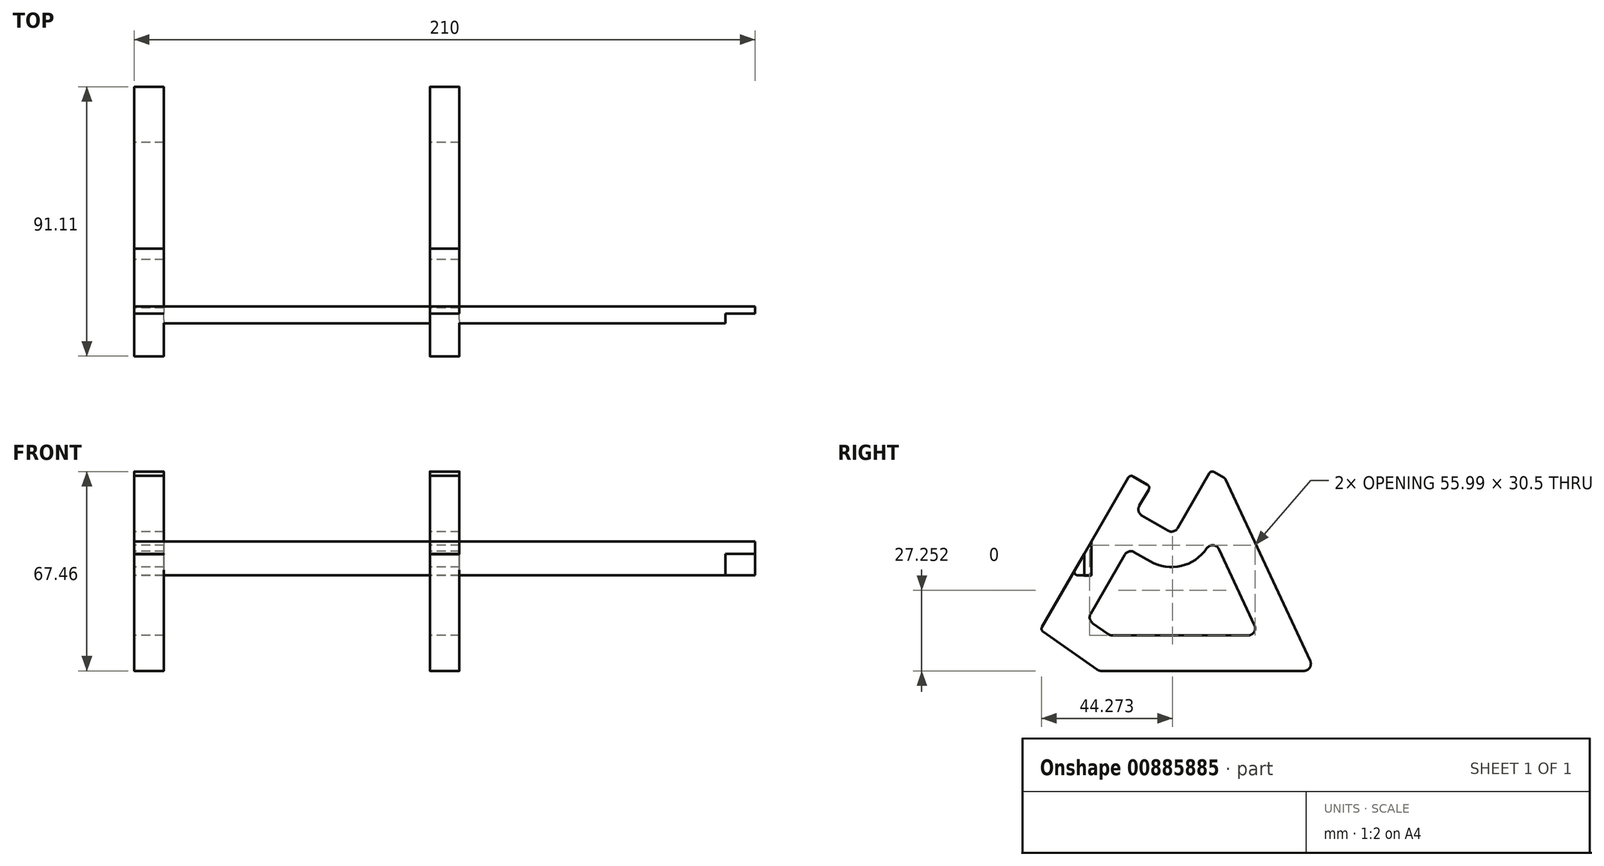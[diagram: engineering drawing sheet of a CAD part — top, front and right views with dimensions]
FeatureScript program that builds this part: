
annotation { "Feature Type Name" : "Feature", "Feature Type Description" : "" }
export const myFeature = defineFeature(function(context is Context, id is Id, definition is map)
    precondition{}
    {
        {
            var Q0;
            Q0=qCreatedBy(makeId("Right.planeOp"),FACE);
            var sketch = newSketch(context, id + "F0", { "sketchPlane" : qUnion([Q0])});
            skLineSegment(sketch, "E0", {"start": v(-36.35, 13.26) * mm, "end": v(-18.04, 0.43) * mm});
            skLineSegment(sketch, "E1", {"start": v(-16.66, 0) * mm, "end": v(-10.97, 0) * mm});
            skLineSegment(sketch, "E2", {"start": v(24.9, 65.35) * mm, "end": v(21.53, 67.3) * mm});
            skLineSegment(sketch, "E3", {"start": v(19.9, 66.86) * mm, "end": v(9.2, 48.33) * mm});
            skLineSegment(sketch, "E4", {"start": v(-3.8, 55.83) * mm, "end": v(-0.6, 61.37) * mm});
            skLineSegment(sketch, "E5", {"start": v(-1.04, 63.01) * mm, "end": v(-5.86, 65.8) * mm});
            skLineSegment(sketch, "E6", {"start": v(-7.54, 65.34) * mm, "end": v(-19.98, 43.8) * mm});
            skLineSegment(sketch, "E7", {"start": v(-2.92, 52.55) * mm, "end": v(5.91, 47.45) * mm});
            skLineSegment(sketch, "E8", {"start": v(10.16, 50) * mm, "end": v(1.5, 50) * mm, "construction": true});
            skPoint(sketch, "E9.visualSharp", {"position": v(8, 46.25) * mm});
            skArc(sketch, "E9.filletArc", {"start": v(5.91, 47.45) * mm, "mid": v(7.73, 47.21) * mm, "end": v(9.2, 48.33) * mm});
            skPoint(sketch, "E10.visualSharp", {"position": v(-5, 53.75) * mm});
            skArc(sketch, "E10.filletArc", {"start": v(-3.8, 55.83) * mm, "mid": v(-4.04, 54) * mm, "end": v(-2.92, 52.55) * mm});
            skPoint(sketch, "E11.visualSharp", {"position": v(25.23, 65.16) * mm});
            skPoint(sketch, "E12.visualSharp", {"position": v(20.5, 67.9) * mm});
            skArc(sketch, "E12.filletArc", {"start": v(21.53, 67.3) * mm, "mid": v(20.62, 67.42) * mm, "end": v(19.9, 66.86) * mm});
            skPoint(sketch, "E13.visualSharp", {"position": v(0, 62.41) * mm});
            skArc(sketch, "E13.filletArc", {"start": v(-0.6, 61.37) * mm, "mid": v(-0.48, 62.28) * mm, "end": v(-1.04, 63.01) * mm});
            skPoint(sketch, "E14.visualSharp", {"position": v(-6.93, 66.41) * mm});
            skArc(sketch, "E14.filletArc", {"start": v(-5.86, 65.8) * mm, "mid": v(-6.8, 65.92) * mm, "end": v(-7.54, 65.34) * mm});
            skPoint(sketch, "E15.visualSharp", {"position": v(-37.25, 13.89) * mm});
            skArc(sketch, "E15.filletArc", {"start": v(-36.7, 14.84) * mm, "mid": v(-36.83, 13.98) * mm, "end": v(-36.35, 13.26) * mm});
            skLineSegment(sketch, "E16", {"start": v(-10.97, 0) * mm, "end": v(21.5, 0) * mm});
            skLineSegment(sketch, "E17", {"start": v(25.4, 64.82) * mm, "end": v(54.02, 3.41) * mm});
            skLineSegment(sketch, "E18", {"start": v(51.85, 0) * mm, "end": v(21.5, 0) * mm});
            skArc(sketch, "E19.filletArc", {"start": v(25.4, 64.82) * mm, "mid": v(25.19, 65.12) * mm, "end": v(24.9, 65.35) * mm});
            skLineSegment(sketch, "E20.0", {"start": v(14.51, 59.75) * mm, "end": v(15.08, 58.53) * mm});
            skLineSegment(sketch, "E21.0", {"start": v(-12.88, 12) * mm, "end": v(33.01, 12) * mm});
            skLineSegment(sketch, "E22.0", {"start": v(-19.56, 16.15) * mm, "end": v(-14.25, 12.43) * mm});
            skLineSegment(sketch, "E23.1", {"start": v(-5.46, 40.16) * mm, "end": v(-0.09, 37.06) * mm});
            skArc(sketch, "E23.2", {"start": v(-0.09, 37.06) * mm, "mid": v(10.34, 35.5) * mm, "end": v(19.04, 41.46) * mm});
            skLineSegment(sketch, "E23.3", {"start": v(28.6, 57.94) * mm, "end": v(27.78, 56.53) * mm});
            skLineSegment(sketch, "E24.trimOffspring", {"start": v(23.2, 41.13) * mm, "end": v(35.19, 15.41) * mm});
            skLineSegment(sketch, "E25.trimOffspring", {"start": v(-8.74, 39.28) * mm, "end": v(-20.26, 19.32) * mm});
            skPoint(sketch, "E26.visualSharp", {"position": v(21.02, 45.8) * mm});
            skArc(sketch, "E26.filletArc", {"start": v(23.2, 41.13) * mm, "mid": v(21.21, 42.5) * mm, "end": v(19.04, 41.46) * mm});
            skPoint(sketch, "E27.visualSharp", {"position": v(36.78, 12) * mm});
            skArc(sketch, "E27.filletArc", {"start": v(33.01, 12) * mm, "mid": v(35.04, 13.11) * mm, "end": v(35.19, 15.41) * mm});
            skPoint(sketch, "E28.visualSharp", {"position": v(-13.63, 12) * mm});
            skArc(sketch, "E28.filletArc", {"start": v(-14.25, 12.43) * mm, "mid": v(-13.6, 12.11) * mm, "end": v(-12.88, 12) * mm});
            skPoint(sketch, "E29.visualSharp", {"position": v(-21.36, 17.41) * mm});
            skArc(sketch, "E29.filletArc", {"start": v(-20.26, 19.32) * mm, "mid": v(-20.53, 17.6) * mm, "end": v(-19.56, 16.15) * mm});
            skPoint(sketch, "E30.visualSharp", {"position": v(-7.54, 41.36) * mm});
            skArc(sketch, "E30.filletArc", {"start": v(-5.46, 40.16) * mm, "mid": v(-7.28, 40.4) * mm, "end": v(-8.74, 39.28) * mm});
            skPoint(sketch, "E31.visualSharp", {"position": v(55.62, 0) * mm});
            skArc(sketch, "E31.filletArc", {"start": v(51.85, 0) * mm, "mid": v(53.87, 1.11) * mm, "end": v(54.02, 3.41) * mm});
            skPoint(sketch, "E32.visualSharp", {"position": v(-17.42, 0) * mm});
            skArc(sketch, "E32.filletArc", {"start": v(-18.04, 0.43) * mm, "mid": v(-17.38, 0.11) * mm, "end": v(-16.66, 0) * mm});
            skLineSegment(sketch, "E33", {"start": v(-19.98, 43.8) * mm, "end": v(-19.98, 32.26) * mm});
            skLineSegment(sketch, "E34", {"start": v(-19.98, 32.26) * mm, "end": v(-22.48, 32.26) * mm});
            skLineSegment(sketch, "E35", {"start": v(-22.48, 32.26) * mm, "end": v(-22.48, 39.48) * mm});
            skLineSegment(sketch, "E36.trimOffspring", {"start": v(-22.48, 39.48) * mm, "end": v(-36.7, 14.84) * mm});
            skSolve(sketch);
        }
        {
            var Q0;
            Q0=makeQuery(id+"F0.imprint","IMPRINT",FACE,{"disambiguationData":[TD([[makeQuery(id+"F0.imprint","IMPRINT",EDGE,{"derivedFrom":sQuery(id+"F0.wireOp",EDGE,"E0")}),1.0]])]});
            extrude(context, id + "F1", {"entities" : qUnion([Q0]), "depth" : 10 * mm, "offsetDistance" : 25 * mm});
        }
        {
            var Q0;
            Q0=makeQuery(id+"F1.opExtrude","CAP_FACE",FACE,{"disambiguationData":[OSD([sQuery(id+"F0.wireOp",EDGE,"E0"),sQuery(id+"F0.wireOp",EDGE,"E1"),sQuery(id+"F0.wireOp",EDGE,"E2"),sQuery(id+"F0.wireOp",EDGE,"E3"),sQuery(id+"F0.wireOp",EDGE,"E4"),sQuery(id+"F0.wireOp",EDGE,"E5"),sQuery(id+"F0.wireOp",EDGE,"E6"),sQuery(id+"F0.wireOp",EDGE,"E7"),sQuery(id+"F0.wireOp",EDGE,"E9.filletArc"),sQuery(id+"F0.wireOp",EDGE,"E10.filletArc"),sQuery(id+"F0.wireOp",EDGE,"E12.filletArc"),sQuery(id+"F0.wireOp",EDGE,"E13.filletArc"),sQuery(id+"F0.wireOp",EDGE,"E14.filletArc"),sQuery(id+"F0.wireOp",EDGE,"E15.filletArc"),sQuery(id+"F0.wireOp",EDGE,"E16"),sQuery(id+"F0.wireOp",EDGE,"E17"),sQuery(id+"F0.wireOp",EDGE,"E18"),sQuery(id+"F0.wireOp",EDGE,"E19.filletArc"),sQuery(id+"F0.wireOp",EDGE,"E21.0"),sQuery(id+"F0.wireOp",EDGE,"E22.0"),sQuery(id+"F0.wireOp",EDGE,"E23.1"),sQuery(id+"F0.wireOp",EDGE,"E23.2"),sQuery(id+"F0.wireOp",EDGE,"E24.trimOffspring"),sQuery(id+"F0.wireOp",EDGE,"E25.trimOffspring"),sQuery(id+"F0.wireOp",EDGE,"E26.filletArc"),sQuery(id+"F0.wireOp",EDGE,"E27.filletArc"),sQuery(id+"F0.wireOp",EDGE,"E28.filletArc"),sQuery(id+"F0.wireOp",EDGE,"E29.filletArc"),sQuery(id+"F0.wireOp",EDGE,"E30.filletArc"),sQuery(id+"F0.wireOp",EDGE,"E31.filletArc"),sQuery(id+"F0.wireOp",EDGE,"E32.filletArc"),sQuery(id+"F0.wireOp",EDGE,"E33"),sQuery(id+"F0.wireOp",EDGE,"E34"),sQuery(id+"F0.wireOp",EDGE,"E35"),sQuery(id+"F0.wireOp",EDGE,"E36.trimOffspring")])],"isStart":true});
            var sketch = newSketch(context, id + "F2", { "sketchPlane" : qUnion([Q0])});
            skLineSegment(sketch, "E37.0", {"start": v(22.43, 32.3) * mm, "end": v(22.43, 39.56) * mm});
            skLineSegment(sketch, "E37.1", {"start": v(20.03, 32.3) * mm, "end": v(22.43, 32.3) * mm});
            skLineSegment(sketch, "E37.2", {"start": v(20.03, 43.72) * mm, "end": v(20.03, 32.3) * mm});
            skLineSegment(sketch, "E38", {"start": v(20.03, 43.72) * mm, "end": v(22.43, 39.56) * mm});
            skSolve(sketch);
        }
        {
            var Q0;
            Q0 = qSketchRegion(id + "F2", true);
            extrude(context, id + "F3", {"entities" : qUnion([Q0]), "operationType" : NewBodyOperationType.ADD, "oppositeDirection" : true, "depth" : 110 * mm, "offsetDistance" : 25 * mm});
        }
        {
            var Q0;
            Q0=makeQuery(id+"F3.opExtrude","CAP_FACE",FACE,{"disambiguationData":[OSD([sQuery(id+"F2.wireOp",EDGE,"E37.0"),sQuery(id+"F2.wireOp",EDGE,"E37.1"),sQuery(id+"F2.wireOp",EDGE,"E37.2"),sQuery(id+"F2.wireOp",EDGE,"E38")])],"isStart":true});
            cPlane(context, id + "F4", {"entities" : qUnion([Q0]), "cplaneType" : CPlaneType.OFFSET, "offset" : 10 * mm, "oppositeDirection" : true, "width" : 150 * mm, "height" : 150 * mm});
        }
        {
            var Q0;
            Q0=qCreatedBy(id+"F4.planeOp",FACE);
            var sketch = newSketch(context, id + "F5", { "sketchPlane" : qUnion([Q0])});
            skLineSegment(sketch, "E39.0", {"start": v(22.43, 32.3) * mm, "end": v(22.43, 39.56) * mm});
            skLineSegment(sketch, "E40", {"start": v(22.43, 39.56) * mm, "end": v(25.58, 34.1) * mm});
            skLineSegment(sketch, "E41", {"start": v(24.54, 32.3) * mm, "end": v(22.43, 32.3) * mm});
            skPoint(sketch, "E42.visualSharp", {"position": v(26.62, 32.3) * mm});
            skArc(sketch, "E42.filletArc", {"start": v(24.54, 32.3) * mm, "mid": v(25.58, 32.9) * mm, "end": v(25.58, 34.1) * mm});
            skSolve(sketch);
        }
        {
            var Q0;
            Q0=makeQuery(id+"F5.imprint","IMPRINT",FACE,{"disambiguationData":[TD([[makeQuery(id+"F5.imprint","IMPRINT",EDGE,{"derivedFrom":sQuery(id+"F5.wireOp",EDGE,"E39.0")}),-1.0]])]});
            extrude(context, id + "F6", {"entities" : qUnion([Q0]), "operationType" : NewBodyOperationType.ADD, "oppositeDirection" : true, "depth" : 90 * mm, "offsetDistance" : 25 * mm});
        }
        {
            var Q0;
            Q0=makeQuery(id+"F1.opExtrude","SWEPT_BODY",BODY,{"disambiguationData":[OSD([sQuery(id+"F0.wireOp",EDGE,"E0"),sQuery(id+"F0.wireOp",EDGE,"E1"),sQuery(id+"F0.wireOp",EDGE,"E2"),sQuery(id+"F0.wireOp",EDGE,"E3"),sQuery(id+"F0.wireOp",EDGE,"E4"),sQuery(id+"F0.wireOp",EDGE,"E5"),sQuery(id+"F0.wireOp",EDGE,"E6"),sQuery(id+"F0.wireOp",EDGE,"E7"),sQuery(id+"F0.wireOp",EDGE,"E9.filletArc"),sQuery(id+"F0.wireOp",EDGE,"E10.filletArc"),sQuery(id+"F0.wireOp",EDGE,"E12.filletArc"),sQuery(id+"F0.wireOp",EDGE,"E13.filletArc"),sQuery(id+"F0.wireOp",EDGE,"E14.filletArc"),sQuery(id+"F0.wireOp",EDGE,"E15.filletArc"),sQuery(id+"F0.wireOp",EDGE,"E16"),sQuery(id+"F0.wireOp",EDGE,"E17"),sQuery(id+"F0.wireOp",EDGE,"E18"),sQuery(id+"F0.wireOp",EDGE,"E19.filletArc"),sQuery(id+"F0.wireOp",EDGE,"E21.0"),sQuery(id+"F0.wireOp",EDGE,"E22.0"),sQuery(id+"F0.wireOp",EDGE,"E23.1"),sQuery(id+"F0.wireOp",EDGE,"E23.2"),sQuery(id+"F0.wireOp",EDGE,"E24.trimOffspring"),sQuery(id+"F0.wireOp",EDGE,"E25.trimOffspring"),sQuery(id+"F0.wireOp",EDGE,"E26.filletArc"),sQuery(id+"F0.wireOp",EDGE,"E27.filletArc"),sQuery(id+"F0.wireOp",EDGE,"E28.filletArc"),sQuery(id+"F0.wireOp",EDGE,"E29.filletArc"),sQuery(id+"F0.wireOp",EDGE,"E30.filletArc"),sQuery(id+"F0.wireOp",EDGE,"E31.filletArc"),sQuery(id+"F0.wireOp",EDGE,"E32.filletArc"),sQuery(id+"F0.wireOp",EDGE,"E33"),sQuery(id+"F0.wireOp",EDGE,"E34"),sQuery(id+"F0.wireOp",EDGE,"E35"),sQuery(id+"F0.wireOp",EDGE,"E36.trimOffspring")])]});
            transform(context, id + "F7", {"entities" : qUnion([Q0]), "transformType" : TransformType.TRANSLATION_3D, "dx" : 100 * mm, "dy" : 0 * mm, "dz" : 0 * mm, "makeCopy" : true});
        }
    });
